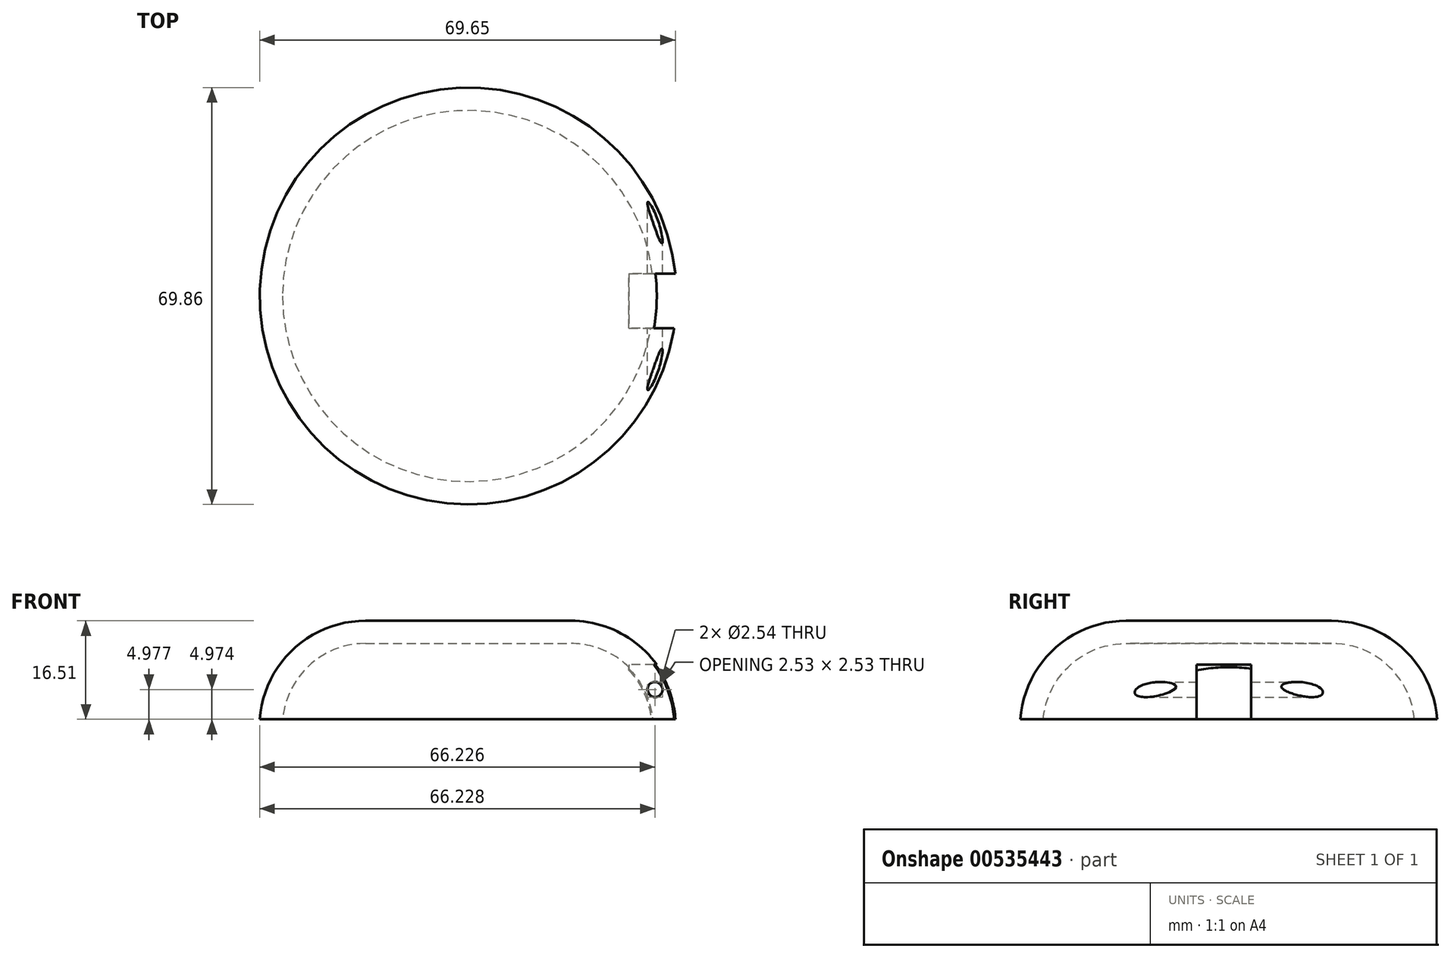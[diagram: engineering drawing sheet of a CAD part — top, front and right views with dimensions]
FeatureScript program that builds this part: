
annotation { "Feature Type Name" : "Feature", "Feature Type Description" : "" }
export const myFeature = defineFeature(function(context is Context, id is Id, definition is map)
    precondition{}
    {
        {
            var Q0;
            Q0=qCreatedBy(makeId("Top.planeOp"),FACE);
            var sketch = newSketch(context, id + "F0", { "sketchPlane" : qUnion([Q0])});
            skCircle(sketch, "E0", {"center": v(0, 0) * mm, "radius": 34.93 * mm});
            skSolve(sketch);
        }
        {
            var Q0;
            Q0 = qSketchRegion(id + "F0", true);
            extrude(context, id + "F1", {"entities" : qUnion([Q0]), "depth" : 16.5 * mm, "offsetDistance" : 25.4 * mm});
        }
        {
            var Q0;
            Q0=makeQuery(id+"F1.opExtrude","CAP_EDGE",EDGE,{"disambiguationData":[OSD([sQuery(id+"F0.wireOp",EDGE,"E0")])],"isStart":false});
            fillet(context, id + "F2", {"entities" : qUnion([Q0]), "radius" : 17.78 * mm, "tangentPropagation" : true, "allowEdgeOverflow" : false});
        }
        {
            var Q0;
            Q0=makeQuery(id+"F1.opExtrude","CAP_FACE",FACE,{"disambiguationData":[OSD([sQuery(id+"F0.wireOp",EDGE,"E0")])],"isStart":true});
            shell(context, id + "F3", {"entities" : qUnion([Q0]), "thickness" : 3.8 * mm});
        }
        {
            var Q0;
            Q0=qCreatedBy(makeId("Top.planeOp"),FACE);
            var sketch = newSketch(context, id + "F4", { "sketchPlane" : qUnion([Q0])});
            skLineSegment(sketch, "E1.bottom", {"start": v(38.27, 3.76) * mm, "end": v(26.95, 3.76) * mm});
            skLineSegment(sketch, "E1.top", {"start": v(38.27, -5.38) * mm, "end": v(26.95, -5.38) * mm});
            skLineSegment(sketch, "E1.left", {"start": v(38.27, 3.76) * mm, "end": v(38.27, -5.38) * mm});
            skLineSegment(sketch, "E1.right", {"start": v(26.95, 3.76) * mm, "end": v(26.95, -5.38) * mm});
            skSolve(sketch);
        }
        {
            var Q0;
            Q0 = qSketchRegion(id + "F4", true);
            extrude(context, id + "F5", {"entities" : qUnion([Q0]), "operationType" : NewBodyOperationType.REMOVE, "depth" : 9.14 * mm, "offsetDistance" : 25.4 * mm});
        }
        {
            var Q0;
            Q0=makeQuery(id+"F5.boolean.opBoolean","COPY",FACE,{"derivedFrom":makeQuery(id+"F5.opExtrude","SWEPT_FACE",FACE,{"disambiguationData":[OSD([sQuery(id+"F4.wireOp",EDGE,"E1.top")])]})});
            var sketch = newSketch(context, id + "F6", { "sketchPlane" : qUnion([Q0])});
            skCircle(sketch, "E2", {"center": v(-31.3, 4.98) * mm, "radius": 1.27 * mm});
            skSolve(sketch);
        }
        {
            var Q0;
            Q0 = qSketchRegion(id + "F6", true);
            extrude(context, id + "F7", {"entities" : qUnion([Q0]), "operationType" : NewBodyOperationType.REMOVE, "oppositeDirection" : true, "depth" : 25.4 * mm, "offsetDistance" : 25.4 * mm, "hasSecondDirection" : true, "secondDirectionOppositeDirection" : false, "secondDirectionDepth" : 25.4 * mm});
        }
    });
